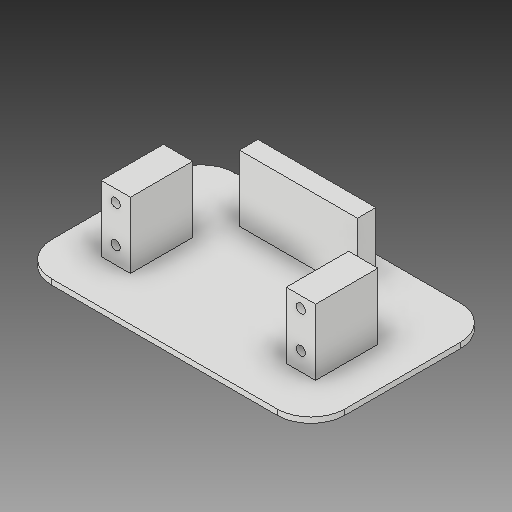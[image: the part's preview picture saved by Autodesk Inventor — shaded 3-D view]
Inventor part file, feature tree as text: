
AUTODESK INVENTOR PART (.ipt)
format: ipt  version: 2017 (Build 210142000, 142)  size: 154,624 bytes
history: native  units: mm
features: sketch x3, extrude x3, projected_geometry x2, fillet x1
ambient origin geometry x8: Origin, YZ Plane, XZ Plane, XY Plane, X Axis, Y Axis, Z Axis, Center Point
bodies: Solid1 (feature_tree)
feature tree (9):
  sketch  "Sketch1"  dims[d0=80.0mm d1=50.0mm]
  sketch  "Sketch2"  dims[d6=80.0mm d7=50.0mm d8=42.5mm d9=12.0mm d10=17.0mm d11=38.0mm d12=1.5mm d13=0.0mm]
  extrude  "Extrusion1"  Depth=50.0mm
  extrude  "Extrusion2"  Depth=1.5mm TaperAngle=0.0deg
  extrude  "Extrusion3"  Depth=8.0mm
  fillet  "Fillet1"  Radius=5.0mm
  sketch  "Sketch3"  dims[d14=18.0mm d15=0.0mm d16=8.0mm d17=5.0mm d18=10.0mm d19=10.0mm d20=2.5mm d21=4.5mm d22=0.0mm d23=9.25mm]
  projected_geometry  "Projected Loop1"
  projected_geometry  "Projected Loop2"
